# Revit family: Faucet-Wall_Mount-Lavatory-KOHLER-Triton_Bowe_Cannock-K-730T70
name_source: partatom
category: Plumbing Fixtures
revit_build: Autodesk Revit 2015 (Build: 20140606_1530(x64)
units: mm (PartAtom-declared; Revit-internal decimal feet)

## types (4) — shared parameters
ADA Compliant = Yes
Assembly Code = D2010
CW Connection = Yes
Cold Water Inlet = Cold Water Inlet
Date Modified = 06/26/2019
Default Elevation = 36"
Drain Included = No
Faucet Hole Spacing = 3"
Flow Rate = 1 GPM
HW Connection = Yes
Handle Clearance = 2 7/16"
Height = 11 1/8"
Hot Water Inlet = Hot Water Inlet
Length = 7 5/16"
Manufacturer = KOHLER Co.
MasterFormat 1995 = 15410
MasterFormat 2004 = 22.41.39
Material = Brass Construction
Pressure = 60.00 psi
Product Documentation Link = https://www.us.kohler.com
Product Name = Triton Bowe Cannock
Product Page URL = http://www.us.kohler.com
Spout Reach = 3 11/16"
URL = https://www.us.kohler.com
Vent Connection = No
Waste Connection = No
Waste Water Outlet = Waste Water Outlet
WaterSense Certified = Yes
Width = 7 3/8"

## per-type parameters (varying)
| type | Description | Finish | Model | Type |
| Service sink faucet, CP-Polished Chrome | Full-flow service sink faucet with 3-11/16 inch gooseneck spout and lever handles | Kohler-Metal-CP-Polished_Chrome | K-730T70-4AR-CP | 1 |
| Service sink faucet, RS-Vibrant Bright Nickel | Full-flow service sink faucet with 3-11/16 inch gooseneck spout and lever handles | KOHLER-Metal-RS-Vibrant_Bright_Nickel | K-730T70-4AR-SR | 2 |
| Bathroom sink faucet, CP-Polished Chrome | 1.2 GPM bathroom sink faucet with 3-11/16 inch gooseneck spout and lever handles, drain not included | Kohler-Metal-CP-Polished_Chrome | K-730T70-4AJR-CP | 3 |
| Bathroom sink faucet, RS-Vibrant Bright Nickel | 1.2 GPM bathroom sink faucet with 3-11/16 inch gooseneck spout and lever handles, drain not included | KOHLER-Metal-RS-Vibrant_Bright_Nickel | K-730T70-4AJR-SR | 4 |

## geometry (parser evidence)
native form markers: Sweep x8
no freeform markers — native parametric forms only
